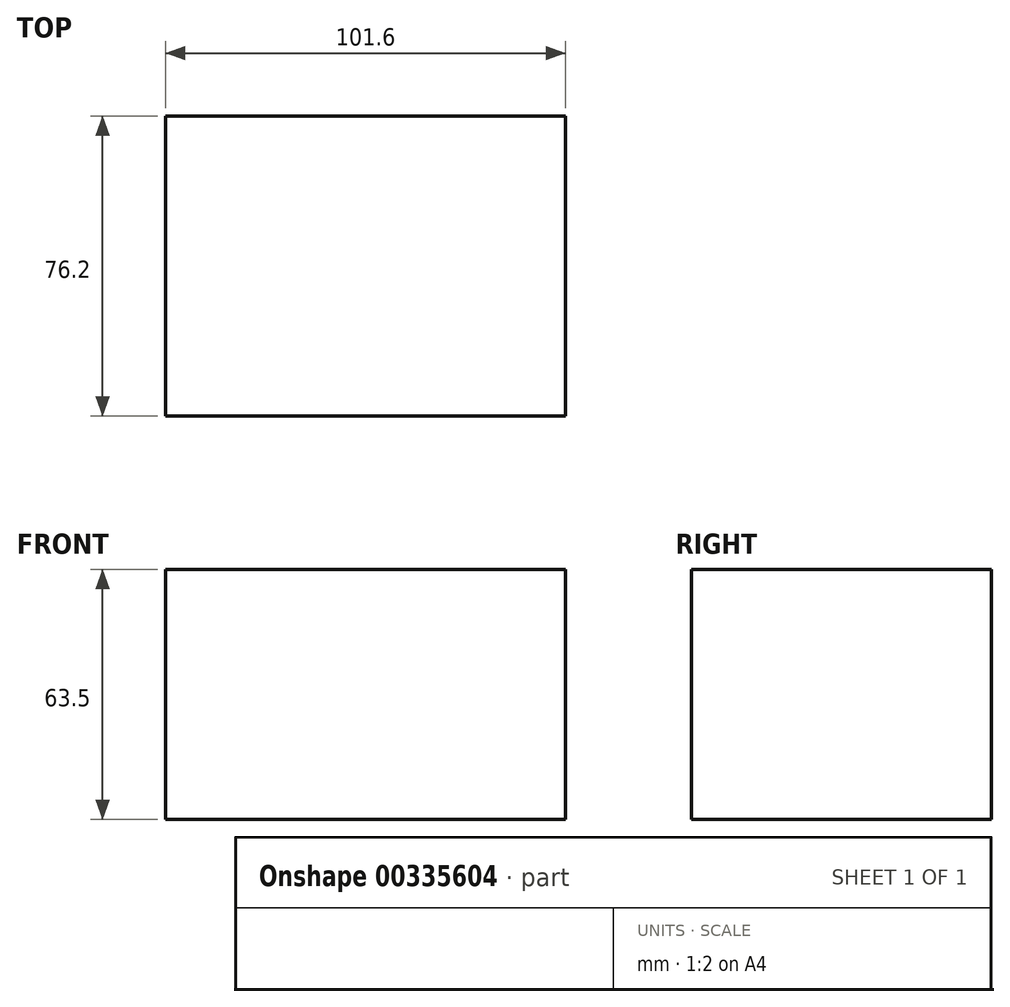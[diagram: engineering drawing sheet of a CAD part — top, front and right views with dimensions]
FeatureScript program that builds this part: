
annotation { "Feature Type Name" : "Feature", "Feature Type Description" : "" }
export const myFeature = defineFeature(function(context is Context, id is Id, definition is map)
    precondition{}
    {
        {
            var Q0;
            Q0=qCreatedBy(makeId("Front.planeOp"),FACE);
            var sketch = newSketch(context, id + "F0", { "sketchPlane" : qUnion([Q0])});
            skLineSegment(sketch, "E0", {"start": v(-38.69, -34.82) * mm, "end": v(62.91, -34.82) * mm});
            skLineSegment(sketch, "E1", {"start": v(62.91, -34.82) * mm, "end": v(62.91, 28.68) * mm});
            skLineSegment(sketch, "E2", {"start": v(62.91, 28.68) * mm, "end": v(-38.69, 28.68) * mm});
            skLineSegment(sketch, "E3", {"start": v(-38.69, 28.68) * mm, "end": v(-38.69, -34.82) * mm});
            skSolve(sketch);
        }
        {
            var Q0;
            Q0=makeQuery(id+"F0.imprint","IMPRINT",FACE,{"disambiguationData":[TD([[makeQuery(id+"F0.imprint","IMPRINT",EDGE,{"derivedFrom":sQuery(id+"F0.wireOp",EDGE,"E0")}),1.0]])]});
            extrude(context, id + "F1", {"entities" : qUnion([Q0]), "depth" : 76.2 * mm});
        }
    });
